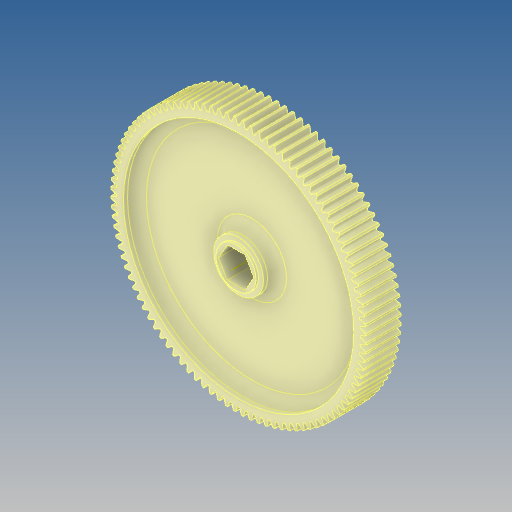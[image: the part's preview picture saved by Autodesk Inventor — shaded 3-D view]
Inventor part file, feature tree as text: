
AUTODESK INVENTOR PART (.ipt)
format: ipt  version: 2020 (Build 240168000, 168)  size: 1,008,640 bytes
history: native  units: in
note: dims shown in document units (in); Inventor stores cm internally (conversion verified against a paired STEP export)
features: mirror x1
ambient origin geometry x8: Origin, YZ Plane, XZ Plane, XY Plane, X Axis, Y Axis, Z Axis, Center Point
bodies: Solid1 (feature_tree)
feature tree (1):
  mirror  "Mirror1"
